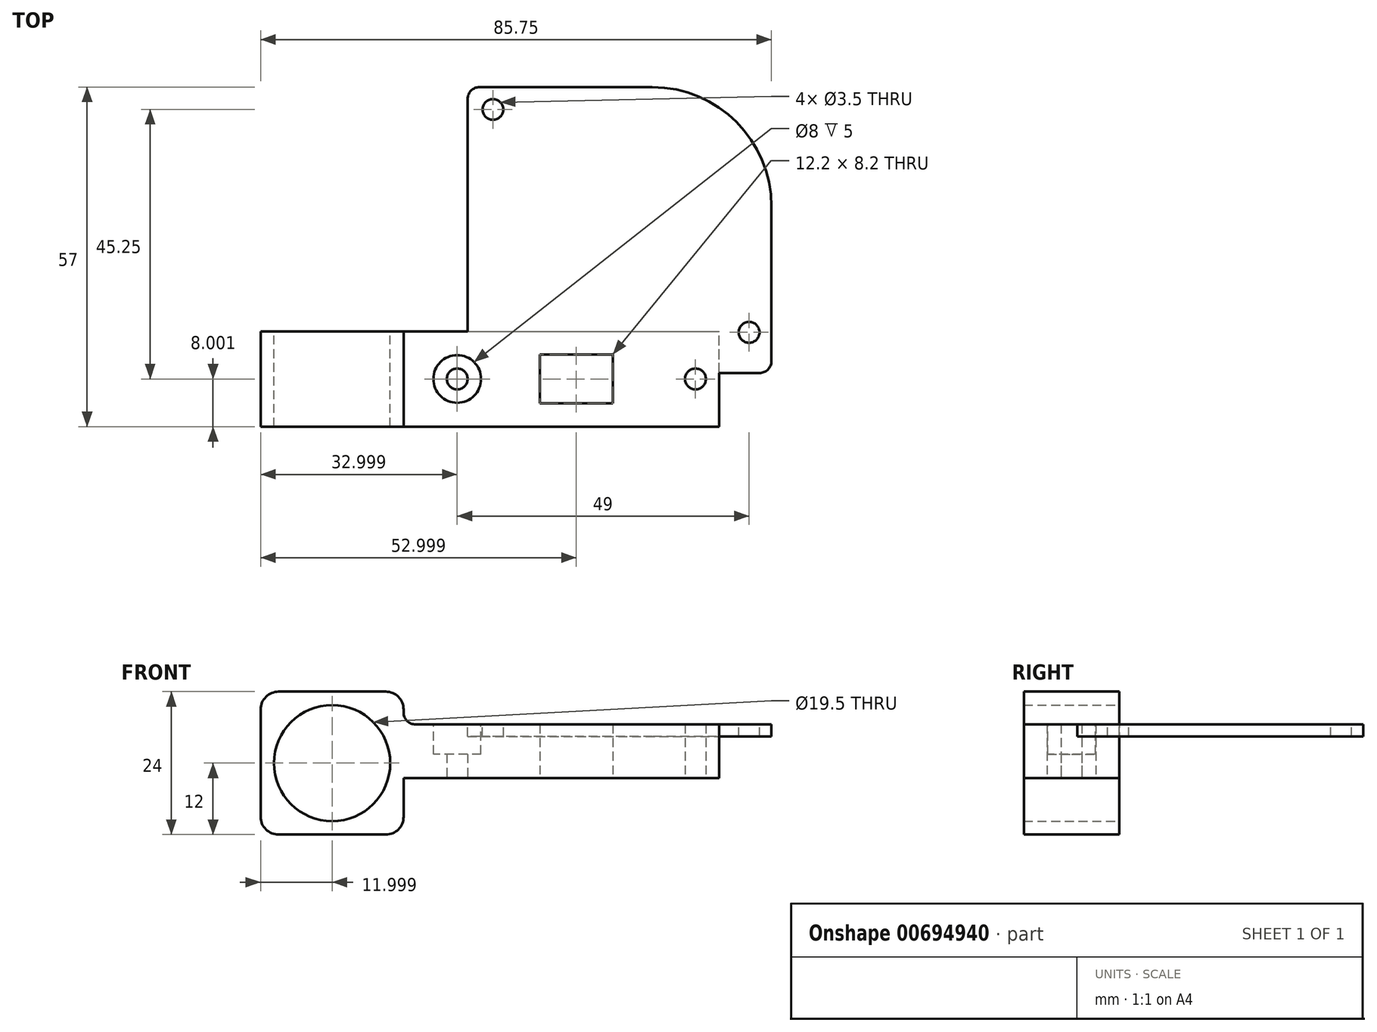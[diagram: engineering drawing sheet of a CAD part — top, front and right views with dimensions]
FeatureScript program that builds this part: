
annotation { "Feature Type Name" : "Feature", "Feature Type Description" : "" }
export const myFeature = defineFeature(function(context is Context, id is Id, definition is map)
    precondition{}
    {
        {
            var Q0;
            Q0=qCreatedBy(makeId("Top.planeOp"),FACE);
            var sketch = newSketch(context, id + "F0", { "sketchPlane" : qUnion([Q0])});
            skLineSegment(sketch, "E0", {"start": v(-33.3, -8.98) * mm, "end": v(-33.3, -24.98) * mm});
            skLineSegment(sketch, "E1", {"start": v(-33.3, -24.98) * mm, "end": v(-24.3, -24.98) * mm});
            skLineSegment(sketch, "E2", {"start": v(-24.3, -24.98) * mm, "end": v(19.7, -24.98) * mm});
            skLineSegment(sketch, "E3", {"start": v(19.7, -24.98) * mm, "end": v(19.7, -8.98) * mm});
            skLineSegment(sketch, "E4", {"start": v(-33.3, -8.98) * mm, "end": v(19.7, -8.98) * mm});
            skLineSegment(sketch, "E5.bottom", {"start": v(-10.4, -21.08) * mm, "end": v(1.8, -21.08) * mm});
            skLineSegment(sketch, "E5.top", {"start": v(-10.4, -12.88) * mm, "end": v(1.8, -12.88) * mm});
            skLineSegment(sketch, "E5.left", {"start": v(-10.4, -21.08) * mm, "end": v(-10.4, -12.88) * mm});
            skLineSegment(sketch, "E5.right", {"start": v(1.8, -21.08) * mm, "end": v(1.8, -12.88) * mm});
            skPoint(sketch, "E5.middle", {"position": v(-4.3, -16.98) * mm});
            skCircle(sketch, "E6", {"center": v(-24.3, -16.98) * mm, "radius": 1.75 * mm});
            skCircle(sketch, "E7", {"center": v(15.7, -16.98) * mm, "radius": 1.75 * mm});
            skSolve(sketch);
        }
        {
            var Q0;
            {var subQ1=sQuery(id+"F0.wireOp",EDGE,"E0");Q0=makeQuery(id+"F0.imprint","IMPRINT",FACE,{"disambiguationData":[TD([[makeQuery(id+"F0.imprint","IMPRINT",EDGE,{"derivedFrom":subQ1}),1.0]])]});}
            extrude(context, id + "F1", {"entities" : qUnion([Q0]), "depth" : 9 * mm, "offsetDistance" : 25 * mm});
        }
        {
            var Q0;
            Q0=makeQuery(id+"F1.opExtrude","SWEPT_FACE",FACE,{"disambiguationData":[OSD([sQuery(id+"F0.wireOp",EDGE,"E4")])]});
            var sketch = newSketch(context, id + "F2", { "sketchPlane" : qUnion([Q0])});
            skLineSegment(sketch, "E8", {"start": v(33.3, 0) * mm, "end": v(33.3, -9.5) * mm});
            skLineSegment(sketch, "E9", {"start": v(33.3, -9.5) * mm, "end": v(57.3, -9.5) * mm});
            skLineSegment(sketch, "E10", {"start": v(57.3, -9.5) * mm, "end": v(57.3, 14.5) * mm});
            skLineSegment(sketch, "E11", {"start": v(57.3, 14.5) * mm, "end": v(33.3, 14.5) * mm});
            skLineSegment(sketch, "E12", {"start": v(33.3, 14.5) * mm, "end": v(33.3, 9) * mm});
            skLineSegment(sketch, "E13", {"start": v(33.3, 9) * mm, "end": v(33.3, 0) * mm});
            skCircle(sketch, "E14", {"center": v(45.3, 2.5) * mm, "radius": 9.75 * mm});
            skPoint(sketch, "E14.centerSnap0", {"position": v(57.3, 2.5) * mm});
            skPoint(sketch, "E14.centerSnap1", {"position": v(45.3, 14.5) * mm});
            skSolve(sketch);
        }
        {
            var Q0;
            Q0=makeQuery(id+"F2.imprint","IMPRINT",FACE,{"disambiguationData":[TD([[makeQuery(id+"F2.imprint","IMPRINT",EDGE,{"derivedFrom":sQuery(id+"F2.wireOp",EDGE,"E8")}),1.0]])]});
            extrude(context, id + "F3", {"entities" : qUnion([Q0]), "oppositeDirection" : true, "depth" : 16 * mm, "offsetDistance" : 25 * mm});
        }
        {
            var Q0;
            Q0=makeQuery(id+"F3.opExtrude","SWEPT_EDGE",EDGE,{"disambiguationData":[OSD([sQuery(id+"F2.wireOp",EDGE,"E11"),sQuery(id+"F2.wireOp",EDGE,"E12")])]});
            var Q1;
            Q1=makeQuery(id+"F3.opExtrude","SWEPT_EDGE",EDGE,{"disambiguationData":[OSD([sQuery(id+"F2.wireOp",EDGE,"E10"),sQuery(id+"F2.wireOp",EDGE,"E11")])]});
            var Q2;
            Q2=makeQuery(id+"F3.opExtrude","SWEPT_EDGE",EDGE,{"disambiguationData":[OSD([sQuery(id+"F2.wireOp",EDGE,"E9"),sQuery(id+"F2.wireOp",EDGE,"E10")])]});
            var Q3;
            Q3=makeQuery(id+"F3.opExtrude","SWEPT_EDGE",EDGE,{"disambiguationData":[OSD([sQuery(id+"F2.wireOp",EDGE,"E8"),sQuery(id+"F2.wireOp",EDGE,"E9")])]});
            fillet(context, id + "F4", {"entities" : qUnion([Q0, Q1, Q2, Q3]), "radius" : 3 * mm, "tangentPropagation" : true, "allowEdgeOverflow" : false});
        }
        {
            var Q0;
            Q0=makeQuery(id+"F1.opExtrude","SWEPT_BODY",BODY,{"disambiguationData":[OSD([sQuery(id+"F0.wireOp",EDGE,"E0"),sQuery(id+"F0.wireOp",EDGE,"E1"),sQuery(id+"F0.wireOp",EDGE,"E2"),sQuery(id+"F0.wireOp",EDGE,"E3"),sQuery(id+"F0.wireOp",EDGE,"E4"),sQuery(id+"F0.wireOp",EDGE,"E5.bottom"),sQuery(id+"F0.wireOp",EDGE,"E5.top"),sQuery(id+"F0.wireOp",EDGE,"E5.left"),sQuery(id+"F0.wireOp",EDGE,"E5.right"),sQuery(id+"F0.wireOp",EDGE,"E6"),sQuery(id+"F0.wireOp",EDGE,"E7")])]});
            var Q1;
            Q1=makeQuery(id+"F3.opExtrude","SWEPT_BODY",BODY,{"disambiguationData":[OSD([sQuery(id+"F2.wireOp",EDGE,"E8"),sQuery(id+"F2.wireOp",EDGE,"E9"),sQuery(id+"F2.wireOp",EDGE,"E10"),sQuery(id+"F2.wireOp",EDGE,"E11"),sQuery(id+"F2.wireOp",EDGE,"E12"),sQuery(id+"F2.wireOp",EDGE,"E13"),sQuery(id+"F2.wireOp",EDGE,"E14")])]});
            booleanBodies(context, id + "F5", {"operationType" : BooleanOperationType.UNION, "tools" : qUnion([Q0, Q1])});
        }
        {
            var Q0;
            {var subQ2=sQuery(id+"F0.wireOp",EDGE,"E0");Q0=makeQuery(id+"F5.opBoolean","SPLIT",EDGE,{"disambiguationData":[topologyDisambiguationEdgeConnected([makeQuery(id+"F3.opExtrude","SWEPT_FACE",FACE,{"disambiguationData":[OSD([sQuery(id+"F2.wireOp",EDGE,"E8"),sQuery(id+"F2.wireOp",EDGE,"E12"),sQuery(id+"F2.wireOp",EDGE,"E13")])]})])],"derivedFrom":makeQuery(id+"F1.opExtrude","CAP_EDGE",EDGE,{"disambiguationData":[OSD([subQ2])],"isStart":true})});}
            var Q1;
            {var subQ0=sQuery(id+"F0.wireOp",EDGE,"E0");Q1=makeQuery(id+"F5.opBoolean","SPLIT",EDGE,{"disambiguationData":[topologyDisambiguationEdgeConnected([makeQuery(id+"F3.opExtrude","SWEPT_FACE",FACE,{"disambiguationData":[OSD([sQuery(id+"F2.wireOp",EDGE,"E8"),sQuery(id+"F2.wireOp",EDGE,"E12"),sQuery(id+"F2.wireOp",EDGE,"E13")])]})])],"derivedFrom":makeQuery(id+"F1.opExtrude","CAP_EDGE",EDGE,{"disambiguationData":[OSD([subQ0])],"isStart":false})});}
            fillet(context, id + "F6", {"entities" : qUnion([Q0, Q1]), "radius" : 2 * mm, "tangentPropagation" : true, "allowEdgeOverflow" : false});
        }
        {
            var Q0;
            Q0=makeQuery(id+"F1.opExtrude","CAP_FACE",FACE,{"disambiguationData":[OSD([sQuery(id+"F0.wireOp",EDGE,"E0"),sQuery(id+"F0.wireOp",EDGE,"E1"),sQuery(id+"F0.wireOp",EDGE,"E2"),sQuery(id+"F0.wireOp",EDGE,"E3"),sQuery(id+"F0.wireOp",EDGE,"E4"),sQuery(id+"F0.wireOp",EDGE,"E5.bottom"),sQuery(id+"F0.wireOp",EDGE,"E5.top"),sQuery(id+"F0.wireOp",EDGE,"E5.left"),sQuery(id+"F0.wireOp",EDGE,"E5.right"),sQuery(id+"F0.wireOp",EDGE,"E6"),sQuery(id+"F0.wireOp",EDGE,"E7")])],"isStart":false});
            var sketch = newSketch(context, id + "F7", { "sketchPlane" : qUnion([Q0])});
            skLineSegment(sketch, "E15", {"start": v(19.7, -15.98) * mm, "end": v(28.45, -15.98) * mm});
            skLineSegment(sketch, "E16", {"start": v(28.45, -15.98) * mm, "end": v(28.45, 32.02) * mm});
            skLineSegment(sketch, "E17", {"start": v(28.45, 32.02) * mm, "end": v(-22.55, 32.02) * mm});
            skLineSegment(sketch, "E18", {"start": v(-22.55, 32.02) * mm, "end": v(-22.55, -8.98) * mm});
            skCircle(sketch, "E19", {"center": v(-18.3, 28.27) * mm, "radius": 1.75 * mm});
            skLineSegment(sketch, "E20", {"start": v(-22.55, -8.98) * mm, "end": v(-22.55, -24.98) * mm, "construction": true});
            skCircle(sketch, "E21", {"center": v(24.7, -9.15) * mm, "radius": 1.75 * mm});
            skLineSegment(sketch, "E22", {"start": v(-18.3, 28.27) * mm, "end": v(24.7, 28.27) * mm, "construction": true});
            skLineSegment(sketch, "E23", {"start": v(24.7, 28.27) * mm, "end": v(24.7, -9.15) * mm, "construction": true});
            skSolve(sketch);
        }
        {
            var Q0;
            Q0 = qSketchRegion(id + "F7", true);
            var Q1;
            {var subQ4=sQuery(id+"F7.wireOp",EDGE,"E15");Q1=makeQuery(id+"F7.imprint","IMPRINT",FACE,{"disambiguationData":[TD([[makeQuery(id+"F7.imprint","IMPRINT",EDGE,{"derivedFrom":subQ4}),1.0]])]});}
            extrude(context, id + "F8", {"entities" : qUnion([Q0, Q1]), "operationType" : NewBodyOperationType.ADD, "oppositeDirection" : true, "depth" : 2 * mm, "offsetDistance" : 25 * mm});
        }
        {
            var Q0;
            Q0=makeQuery(id+"F7.imprint","IMPRINT",FACE,{"disambiguationData":[TD([[makeQuery(id+"F7.imprint","IMPRINT",EDGE,{"derivedFrom":sQuery(id+"F7.wireOp",EDGE,"E19")}),1.0]])]});
            var Q1;
            Q1=makeQuery(id+"F7.imprint","IMPRINT",FACE,{"disambiguationData":[TD([[makeQuery(id+"F7.imprint","IMPRINT",EDGE,{"derivedFrom":sQuery(id+"F7.wireOp",EDGE,"E21")}),1.0]])]});
            extrude(context, id + "F9", {"entities" : qUnion([Q0, Q1]), "operationType" : NewBodyOperationType.REMOVE, "endBound" : BoundingType.UP_TO_NEXT, "oppositeDirection" : true, "depth" : 25 * mm, "offsetDistance" : 25 * mm});
        }
        {
            var Q0;
            Q0=makeQuery(id+"F8.opExtrude","SWEPT_EDGE",EDGE,{"disambiguationData":[OSD([sQuery(id+"F7.wireOp",EDGE,"E17"),sQuery(id+"F7.wireOp",EDGE,"E18")])]});
            var Q1;
            Q1=makeQuery(id+"F8.opExtrude","SWEPT_EDGE",EDGE,{"disambiguationData":[OSD([sQuery(id+"F7.wireOp",EDGE,"E15"),sQuery(id+"F7.wireOp",EDGE,"E16")])]});
            fillet(context, id + "F10", {"entities" : qUnion([Q0, Q1]), "radius" : 2 * mm, "tangentPropagation" : true, "allowEdgeOverflow" : false});
        }
        {
            var Q0;
            Q0=makeQuery(id+"F8.opExtrude","SWEPT_EDGE",EDGE,{"disambiguationData":[OSD([sQuery(id+"F7.wireOp",EDGE,"E16"),sQuery(id+"F7.wireOp",EDGE,"E17")])]});
            fillet(context, id + "F11", {"entities" : qUnion([Q0]), "radius" : 20 * mm, "tangentPropagation" : true, "allowEdgeOverflow" : false});
        }
        {
            var Q0;
            {var subQ0=sQuery(id+"F0.wireOp",EDGE,"E4");var subQ1=sQuery(id+"F0.wireOp",EDGE,"E3");Q0=makeQuery(id+"F8.boolean.opBoolean","MERGE",FACE,{"derivedFrom":[makeQuery(id+"F1.opExtrude","CAP_FACE",FACE,{"disambiguationData":[OSD([sQuery(id+"F0.wireOp",EDGE,"E0"),sQuery(id+"F0.wireOp",EDGE,"E1"),sQuery(id+"F0.wireOp",EDGE,"E2"),subQ1,subQ0,sQuery(id+"F0.wireOp",EDGE,"E5.bottom"),sQuery(id+"F0.wireOp",EDGE,"E5.top"),sQuery(id+"F0.wireOp",EDGE,"E5.left"),sQuery(id+"F0.wireOp",EDGE,"E5.right"),sQuery(id+"F0.wireOp",EDGE,"E6"),sQuery(id+"F0.wireOp",EDGE,"E7")])],"isStart":false}),makeQuery(id+"F8.opExtrude","CAP_FACE",FACE,{"disambiguationData":[OSD([subQ1,subQ0,sQuery(id+"F7.wireOp",EDGE,"E15"),sQuery(id+"F7.wireOp",EDGE,"E16"),sQuery(id+"F7.wireOp",EDGE,"E17"),sQuery(id+"F7.wireOp",EDGE,"E18")])],"isStart":true})]});}
            var sketch = newSketch(context, id + "F12", { "sketchPlane" : qUnion([Q0])});
            skCircle(sketch, "E24", {"center": v(-24.3, -16.98) * mm, "radius": 1.75 * mm});
            skSolve(sketch);
        }
        {
            var Q0;
            Q0=sQuery(id+"F12.wireOp",VERTEX,"E24.center");
            var Q1;
            Q1=makeQuery(id+"F1.opExtrude","SWEPT_BODY",BODY,{"disambiguationData":[OSD([sQuery(id+"F0.wireOp",EDGE,"E0"),sQuery(id+"F0.wireOp",EDGE,"E1"),sQuery(id+"F0.wireOp",EDGE,"E2"),sQuery(id+"F0.wireOp",EDGE,"E3"),sQuery(id+"F0.wireOp",EDGE,"E4"),sQuery(id+"F0.wireOp",EDGE,"E5.bottom"),sQuery(id+"F0.wireOp",EDGE,"E5.top"),sQuery(id+"F0.wireOp",EDGE,"E5.left"),sQuery(id+"F0.wireOp",EDGE,"E5.right"),sQuery(id+"F0.wireOp",EDGE,"E6"),sQuery(id+"F0.wireOp",EDGE,"E7")])]});
            hole(context, id + "F13", {"style" : HoleStyle.C_BORE, "endStyle" : HoleEndStyle.THROUGH, "holeDiameter" : 3.5 * mm, "cBoreDiameter" : 8 * mm, "cBoreDepth" : 5 * mm, "majorDiameter" : 5 * mm, "isTappedThrough" : true, "tappedDepth" : 12 * mm, "tapClearance" : 3, "locations" : qUnion([Q0]), "scope" : qUnion([Q1])});
        }
    });
